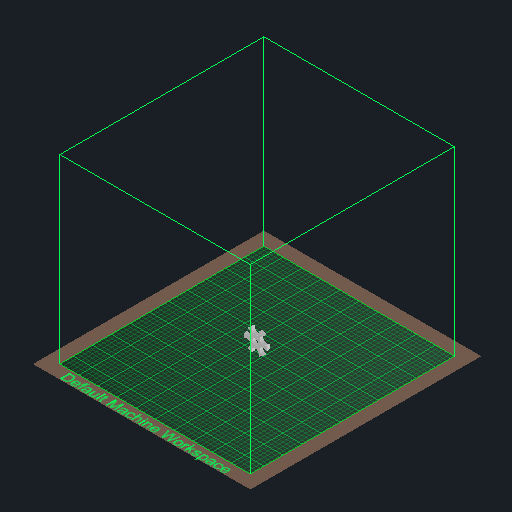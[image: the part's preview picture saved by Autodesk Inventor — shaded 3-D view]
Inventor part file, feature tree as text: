
AUTODESK INVENTOR PART (.ipt)
format: ipt  version: 2022.2 (Build 262287010, 287A)  size: 419,328 bytes
history: native  units: mm
features: extrude x6, sketch x6, pattern_circular x2
ambient origin geometry x8: Origin, YZ Plane, XZ Plane, XY Plane, X Axis, Y Axis, Z Axis, Center Point
bodies: Solid1 (feature_tree)
feature tree (14):
  extrude  "Extrusion1"  Depth=8.0mm TaperAngle=0.0deg
  extrude  "Extrusion2"  Depth=17.5mm
  extrude  "Extrusion3"  Depth=16.0mm
  pattern_circular  "Circular Pattern1"  Count=6 Angle=360.0deg
  extrude  "Extrusion6"  Depth=5.0mm TaperAngle=0.0deg
  pattern_circular  "Circular Pattern2"  [2 undecoded]
  extrude  "Extrusion4"  Depth=6.0mm TaperAngle=360.0deg
  extrude  "Extrusion7"  Depth=6.0mm
  sketch  "Sketch1"  dims[d0=60.0mm d1=8.0mm d2=0.0mm]
  sketch  "Sketch2"  dims[d3=17.5mm d4=20.5mm]
  sketch  "Sketch3"  dims[d5=1.4mm d6=0.0mm d7=16.0mm]
  sketch  "Sketch4"  dims[d8=0.0mm d9=0.0mm d10=60.0mm d11=360.0deg]
  sketch  "Sketch7"  dims[d13=7.0mm d14=5.0mm d15=0.0mm]
  sketch  "Sketch8"  dims[d19=17.5mm d20=20.5mm d21=60.0mm d23=360.0deg d25=15.0mm d26=20.5mm d27=80.0mm d29=360.0deg d32=17.5mm d33=17.5mm d34=10.0mm d35=0.0mm d36=60.0mm d37=360.0deg d39=19.0mm d40=6.0mm d41=0.0mm]
note: 2 required parameter values undecoded (feature->parameter linkage not recoverable at this tier; creation-order binding heuristic only, values carry confidence <= 0.55)
